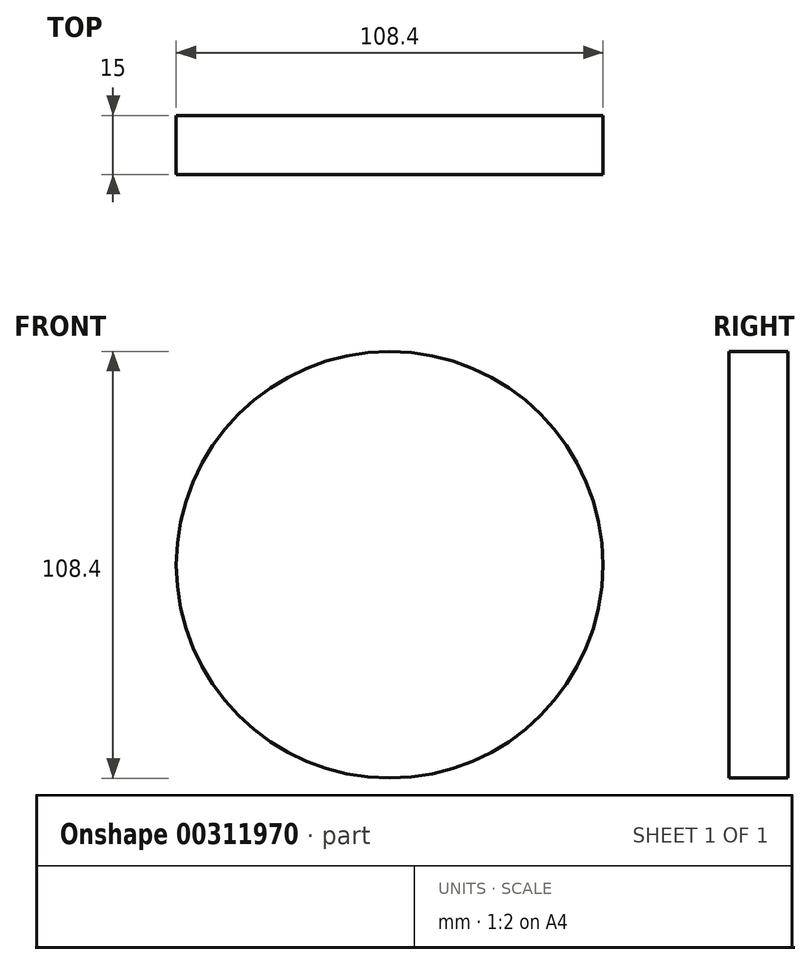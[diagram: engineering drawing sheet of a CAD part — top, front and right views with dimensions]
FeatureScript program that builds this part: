
annotation { "Feature Type Name" : "Feature", "Feature Type Description" : "" }
export const myFeature = defineFeature(function(context is Context, id is Id, definition is map)
    precondition{}
    {
        {
            var Q0;
            Q0=qCreatedBy(makeId("Front.planeOp"),FACE);
            var sketch = newSketch(context, id + "F0", { "sketchPlane" : qUnion([Q0])});
            skCircle(sketch, "E0", {"center": v(0, 0) * mm, "radius": 54.2 * mm});
            skLineSegment(sketch, "E1", {"start": v(0, 0) * mm, "end": v(-42.13, 0) * mm, "construction": true});
            skSolve(sketch);
        }
        {
            var Q0;
            Q0=makeQuery(id+"F0.imprint","IMPRINT",FACE,{"disambiguationData":[TD([[makeQuery(id+"F0.imprint","IMPRINT",EDGE,{"derivedFrom":sQuery(id+"F0.wireOp",EDGE,"E0")}),1.0]])]});
            extrude(context, id + "F1", {"entities" : qUnion([Q0]), "depth" : 15 * mm, "offsetDistance" : 25 * mm});
        }
    });
